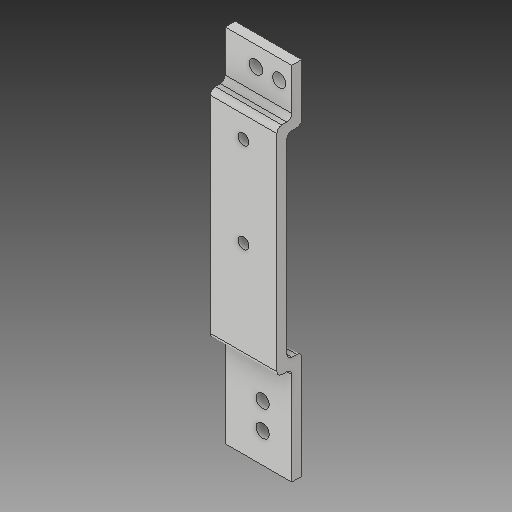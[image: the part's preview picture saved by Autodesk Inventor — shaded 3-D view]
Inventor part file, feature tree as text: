
AUTODESK INVENTOR PART (.ipt)
format: ipt  version: 2018 (Build 220112000, 112)  size: 152,064 bytes
history: native  units: mm
features: reference x9, extrude x5, sketch x5, fillet x1
ambient origin geometry x8: Origin, YZ Plane, XZ Plane, XY Plane, X Axis, Y Axis, Z Axis, Center Point
bodies: Solid1 (feature_tree)
feature tree (20):
  extrude  "Extrusion1"  Depth=130.0mm
  extrude  "Extrusion2"  Depth=6.0mm TaperAngle=0.0deg
  extrude  "Extrusion3"  Depth=6.0mm
  extrude  "Extrusion4"  Depth=34.0mm
  fillet  "Fillet1"  Radius=65.0mm
  extrude  "Extrusion5"  Depth=40.0mm
  sketch  "Sketch1"  dims[d0=40.0mm d1=130.0mm]
  sketch  "Sketch2"  dims[d2=6.0mm d3=0.0mm d4=6.0mm d5=0.0mm]
  reference  "Reference1"
  reference  "Reference2"
  sketch  "Sketch3"  dims[d6=6.0mm d7=6.0mm]
  sketch  "Sketch4"  dims[d8=3.0mm d9=0.0mm d10=34.0mm d11=65.0mm]
  sketch  "Sketch5"  dims[d12=40.0mm d13=40.0mm d14=6.0mm d15=0.0mm d16=3.0mm d17=8.0mm d18=6.0mm d19=0.0mm]
  reference  "Reference3"
  reference  "Reference4"
  reference  "Reference5"
  reference  "Reference6"
  reference  "Reference7"
  reference  "Reference8"
  reference  "Reference9"
